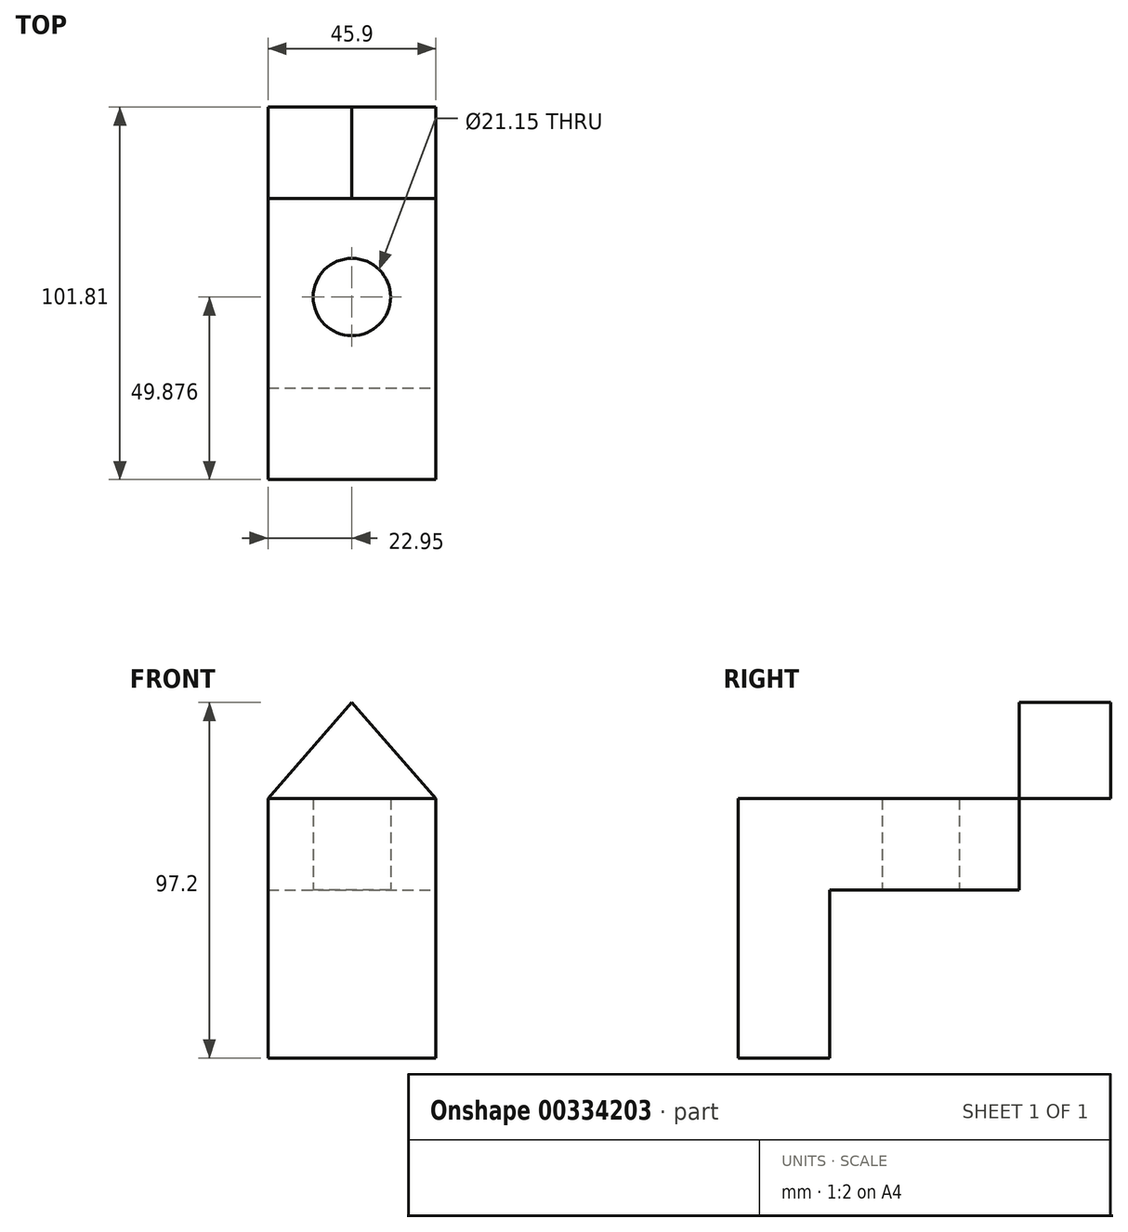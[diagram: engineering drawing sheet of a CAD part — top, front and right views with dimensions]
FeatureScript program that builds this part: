
annotation { "Feature Type Name" : "Feature", "Feature Type Description" : "" }
export const myFeature = defineFeature(function(context is Context, id is Id, definition is map)
    precondition{}
    {
        {
            var Q0;
            Q0=qCreatedBy(makeId("Front.planeOp"),FACE);
            var sketch = newSketch(context, id + "F0", { "sketchPlane" : qUnion([Q0])});
            skLineSegment(sketch, "E0.bottom", {"start": v(-22.95, 22.95) * mm, "end": v(22.95, 22.95) * mm});
            skLineSegment(sketch, "E0.top", {"start": v(-22.95, -22.95) * mm, "end": v(22.95, -22.95) * mm});
            skLineSegment(sketch, "E0.left", {"start": v(-22.95, 22.95) * mm, "end": v(-22.95, -22.95) * mm});
            skLineSegment(sketch, "E0.right", {"start": v(22.95, 22.95) * mm, "end": v(22.95, -22.95) * mm});
            skPoint(sketch, "E0.middle", {"position": v(0, 0) * mm});
            skSolve(sketch);
        }
        {
            var Q0;
            Q0 = qSketchRegion(id + "F0", true);
            extrude(context, id + "F1", {"entities" : qUnion([Q0]), "depth" : 25 * mm});
        }
        {
            var Q0;
            Q0=makeQuery(id+"F1.opExtrude","SWEPT_FACE",FACE,{"disambiguationData":[OSD([sQuery(id+"F0.wireOp",EDGE,"E0.bottom")])]});
            var sketch = newSketch(context, id + "F2", { "sketchPlane" : qUnion([Q0])});
            skLineSegment(sketch, "E1.bottom", {"start": v(-22.95, -25) * mm, "end": v(22.95, -25) * mm});
            skLineSegment(sketch, "E1.top", {"start": v(-22.95, 51.81) * mm, "end": v(22.95, 51.81) * mm});
            skLineSegment(sketch, "E1.left", {"start": v(-22.95, -25) * mm, "end": v(-22.95, 51.81) * mm});
            skLineSegment(sketch, "E1.right", {"start": v(22.95, -25) * mm, "end": v(22.95, 51.81) * mm});
            skLineSegment(sketch, "E2", {"start": v(0, 51.81) * mm, "end": v(0, -25) * mm, "construction": true});
            skCircle(sketch, "E3", {"center": v(0, 24.88) * mm, "radius": 10.57 * mm});
            skSolve(sketch);
        }
        {
            var Q0;
            Q0 = qSketchRegion(id + "F2", true);
            extrude(context, id + "F3", {"entities" : qUnion([Q0]), "operationType" : NewBodyOperationType.ADD, "depth" : 25 * mm});
        }
        {
            var Q0;
            Q0=makeQuery(id+"F3.opExtrude","SWEPT_FACE",FACE,{"disambiguationData":[OSD([sQuery(id+"F2.wireOp",EDGE,"E1.top")])]});
            var sketch = newSketch(context, id + "F4", { "sketchPlane" : qUnion([Q0])});
            skLineSegment(sketch, "E4", {"start": v(-22.95, 47.95) * mm, "end": v(0, 74.25) * mm});
            skLineSegment(sketch, "E5", {"start": v(0, 74.25) * mm, "end": v(22.95, 47.95) * mm});
            skLineSegment(sketch, "E6", {"start": v(22.95, 47.95) * mm, "end": v(-20.02, 47.95) * mm});
            skSolve(sketch);
        }
        {
            var Q0;
            Q0 = qSketchRegion(id + "F4", true);
            var Q1;
            {var subQ0=sQuery(id+"F4.wireOp",EDGE,"E4");Q1=makeQuery(id+"F4.imprint","IMPRINT",FACE,{"disambiguationData":[TD([[makeQuery(id+"F4.imprint","IMPRINT",EDGE,{"derivedFrom":subQ0}),-1.0]])]});}
            extrude(context, id + "F5", {"entities" : qUnion([Q0, Q1]), "depth" : 25 * mm});
        }
    });
